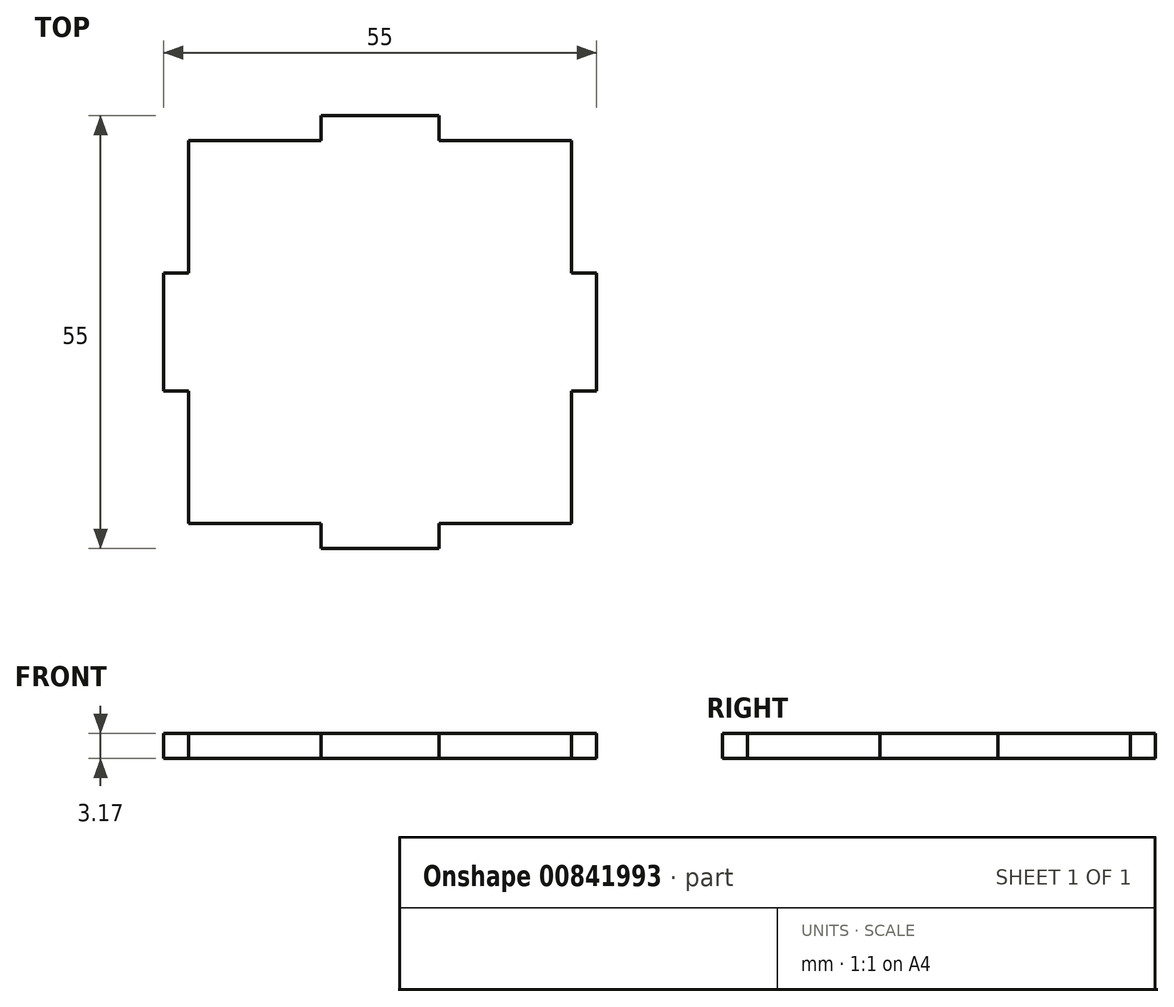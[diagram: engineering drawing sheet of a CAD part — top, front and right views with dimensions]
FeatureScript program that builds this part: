
annotation { "Feature Type Name" : "Feature", "Feature Type Description" : "" }
export const myFeature = defineFeature(function(context is Context, id is Id, definition is map)
    precondition{}
    {
        {
            assignVariable(context, id + "F0", {"name" : "mat_t", "anyValue" : 3.17});
        }
        {
            var Q0;
            Q0=qCreatedBy(makeId("Top.planeOp"),FACE);
            var sketch = newSketch(context, id + "F1", { "sketchPlane" : qUnion([Q0])});
            skLineSegment(sketch, "E0.bottom", {"start": v(24.33, -24.32) * mm, "end": v(-24.32, -24.33) * mm});
            skLineSegment(sketch, "E0.top", {"start": v(24.32, 24.33) * mm, "end": v(-24.33, 24.32) * mm});
            skLineSegment(sketch, "E0.left", {"start": v(24.33, -24.33) * mm, "end": v(24.32, 24.33) * mm});
            skLineSegment(sketch, "E0.right", {"start": v(-24.33, -24.33) * mm, "end": v(-24.33, 24.32) * mm});
            skPoint(sketch, "E0.middle", {"position": v(0, 0) * mm});
            skSolve(sketch);
        }
        {
            var Q0;
            Q0 = qSketchRegion(id + "F1", true);
            extrude(context, id + "F2", {"entities" : qUnion([Q0]), "depth" : (getVariable(context, 'mat_t')) * mm, "offsetDistance" : 25 * mm});
        }
        {
            var Q0;
            Q0=makeQuery(id+"F2.opExtrude","CAP_FACE",FACE,{"disambiguationData":[OSD([sQuery(id+"F1.wireOp",EDGE,"E0.bottom"),sQuery(id+"F1.wireOp",EDGE,"E0.top"),sQuery(id+"F1.wireOp",EDGE,"E0.left"),sQuery(id+"F1.wireOp",EDGE,"E0.right")])],"isStart":false});
            var sketch = newSketch(context, id + "F3", { "sketchPlane" : qUnion([Q0])});
            skLineSegment(sketch, "E1", {"start": v(0, 24.33) * mm, "end": v(0, -24.32) * mm, "construction": true});
            skLineSegment(sketch, "E2", {"start": v(-24.33, 0) * mm, "end": v(24.32, 0) * mm, "construction": true});
            skLineSegment(sketch, "E3.bottom", {"start": v(-24.33, 7.5) * mm, "end": v(-27.5, 7.5) * mm});
            skLineSegment(sketch, "E3.top", {"start": v(-24.33, -7.5) * mm, "end": v(-27.5, -7.5) * mm});
            skLineSegment(sketch, "E3.left", {"start": v(-24.33, 7.5) * mm, "end": v(-24.33, -7.5) * mm});
            skLineSegment(sketch, "E3.right", {"start": v(-27.5, 7.5) * mm, "end": v(-27.5, -7.5) * mm});
            skLineSegment(sketch, "E4.bottom", {"start": v(-7.5, 24.33) * mm, "end": v(7.5, 24.33) * mm});
            skLineSegment(sketch, "E4.top", {"start": v(-7.5, 27.5) * mm, "end": v(7.5, 27.5) * mm});
            skLineSegment(sketch, "E4.left", {"start": v(-7.5, 24.33) * mm, "end": v(-7.5, 27.5) * mm});
            skLineSegment(sketch, "E4.right", {"start": v(7.5, 24.33) * mm, "end": v(7.5, 27.5) * mm});
            skLineSegment(sketch, "E5.MirrorCS", {"start": v(7.5, -24.32) * mm, "end": v(7.5, -27.5) * mm});
            skLineSegment(sketch, "E6.MirrorCS", {"start": v(-7.5, -24.33) * mm, "end": v(-7.5, -27.5) * mm});
            skLineSegment(sketch, "E7.MirrorCS", {"start": v(-7.5, -24.33) * mm, "end": v(7.5, -24.32) * mm});
            skLineSegment(sketch, "E8.MirrorCS", {"start": v(-7.5, -27.5) * mm, "end": v(7.5, -27.5) * mm});
            skLineSegment(sketch, "E9.MirrorCS", {"start": v(27.5, 7.5) * mm, "end": v(27.5, -7.5) * mm});
            skLineSegment(sketch, "E10.MirrorCS", {"start": v(24.32, -7.5) * mm, "end": v(27.5, -7.5) * mm});
            skLineSegment(sketch, "E11.MirrorCS", {"start": v(24.32, 7.5) * mm, "end": v(24.32, -7.5) * mm});
            skLineSegment(sketch, "E12.MirrorCS", {"start": v(24.32, 7.5) * mm, "end": v(27.5, 7.5) * mm});
            skSolve(sketch);
        }
        {
            var Q0;
            Q0 = qSketchRegion(id + "F3", true);
            var Q1;
            Q1=makeQuery(id+"F2.opExtrude","CAP_FACE",FACE,{"disambiguationData":[OSD([sQuery(id+"F1.wireOp",EDGE,"E0.bottom"),sQuery(id+"F1.wireOp",EDGE,"E0.top"),sQuery(id+"F1.wireOp",EDGE,"E0.left"),sQuery(id+"F1.wireOp",EDGE,"E0.right")])],"isStart":true});
            extrude(context, id + "F4", {"entities" : qUnion([Q0]), "operationType" : NewBodyOperationType.ADD, "endBound" : BoundingType.UP_TO_SURFACE, "oppositeDirection" : true, "depth" : 25 * mm, "endBoundEntityFace" : qUnion([Q1]), "offsetDistance" : 25 * mm});
        }
    });
